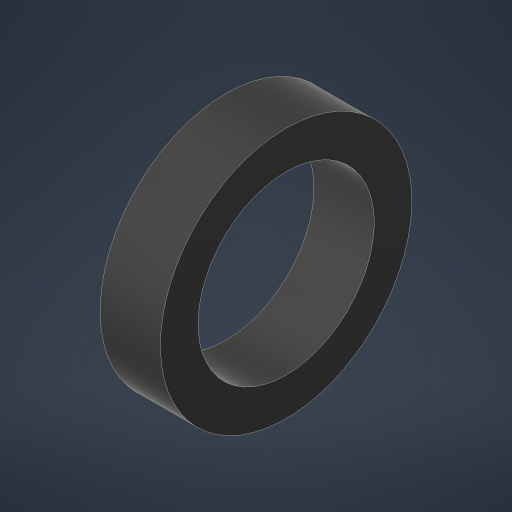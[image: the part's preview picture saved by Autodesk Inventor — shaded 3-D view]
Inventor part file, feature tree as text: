
AUTODESK INVENTOR PART (.ipt)
format: ipt  version: 2023.4 (Build 274418000, 418)  size: 173,056 bytes
history: native  units: in
note: dims shown in document units (in); Inventor stores cm internally (conversion verified against a paired STEP export)
features: extrude x1, sketch x1
ambient origin geometry x8: Origin, YZ Plane, XZ Plane, XY Plane, X Axis, Y Axis, Z Axis, Center Point
bodies: Solid1 (feature_tree)
feature tree (2):
  extrude  "Extrusion1"  Depth=0.2in
  sketch  "Sketch1"  dims[d0=0.585in d1=0.125in d2=0.2in d3=0.0in]
